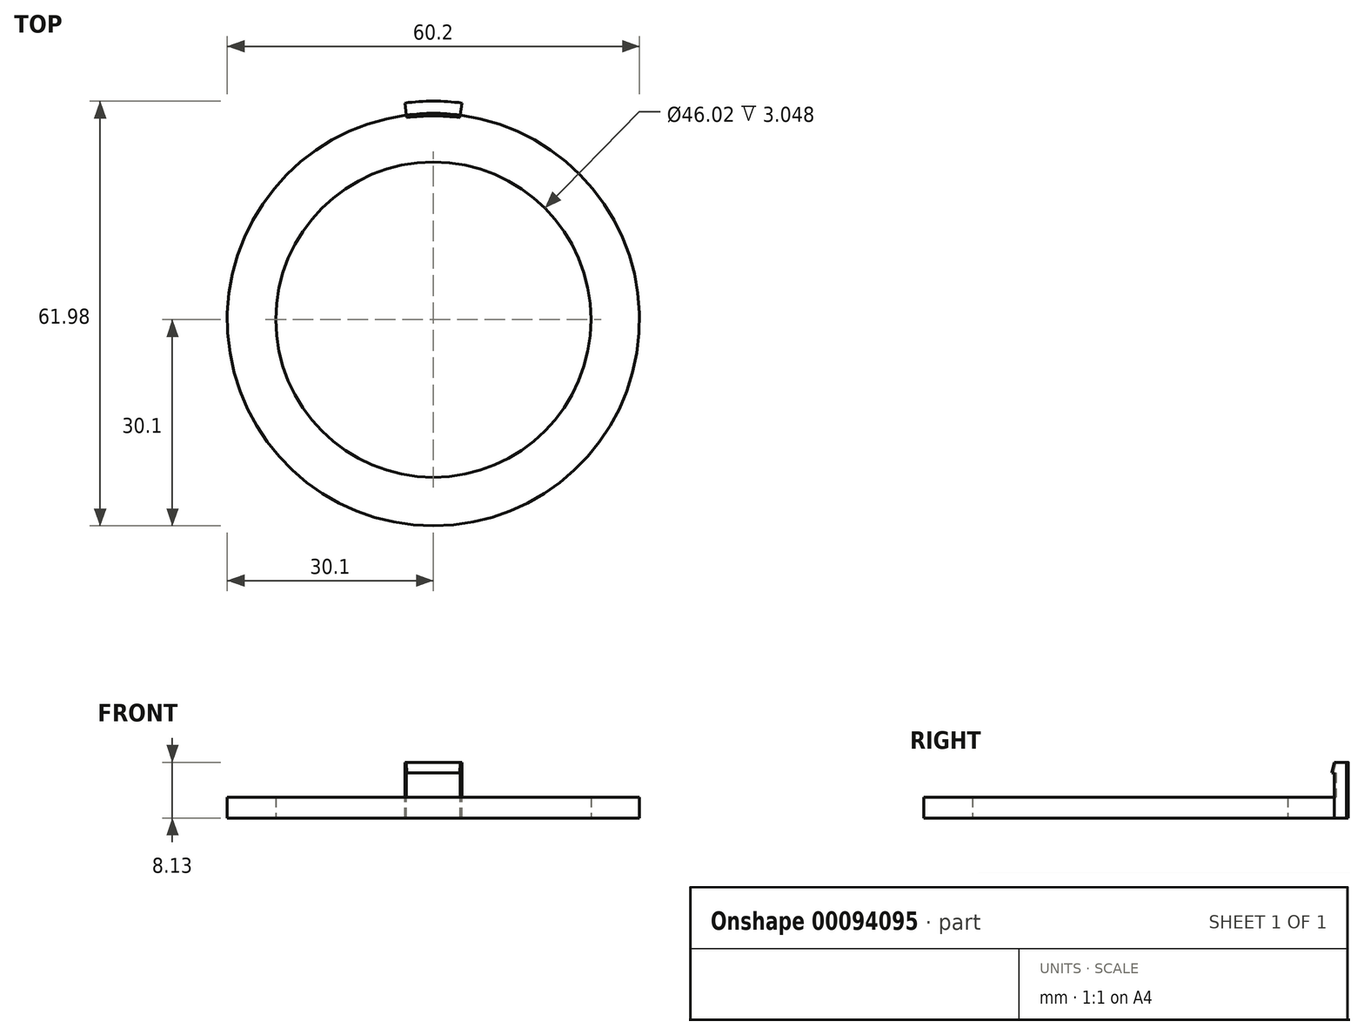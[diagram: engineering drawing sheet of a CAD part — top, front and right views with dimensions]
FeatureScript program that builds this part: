
annotation { "Feature Type Name" : "Feature", "Feature Type Description" : "" }
export const myFeature = defineFeature(function(context is Context, id is Id, definition is map)
    precondition{}
    {
        {
            var Q0;
            Q0=qCreatedBy(makeId("Top.planeOp"),FACE);
            var sketch = newSketch(context, id + "F0", { "sketchPlane" : qUnion([Q0])});
            skCircle(sketch, "E0", {"center": v(0, 0) * mm, "radius": 23.01 * mm});
            skCircle(sketch, "E1", {"center": v(0, 0) * mm, "radius": 30.1 * mm});
            skSolve(sketch);
        }
        {
            var Q0;
            Q0=makeQuery(id+"F0.imprint","IMPRINT",FACE,{"disambiguationData":[TD([[makeQuery(id+"F0.imprint","IMPRINT",EDGE,{"derivedFrom":sQuery(id+"F0.wireOp",EDGE,"E0")}),-1.0]])]});
            extrude(context, id + "F1", {"entities" : qUnion([Q0]), "depth" : 3.05 * mm, "offsetDistance" : 25.4 * mm});
        }
        {
            var Q0;
            Q0=qCreatedBy(makeId("Right.planeOp"),FACE);
            var sketch = newSketch(context, id + "F2", { "sketchPlane" : qUnion([Q0])});
            skLineSegment(sketch, "E2", {"start": v(-23.01, 3.05) * mm, "end": v(-30.1, 3.05) * mm});
            skLineSegment(sketch, "E3", {"start": v(30.1, 3.05) * mm, "end": v(23.01, 3.05) * mm});
            skLineSegment(sketch, "E4", {"start": v(30.1, 3.05) * mm, "end": v(30.1, 0) * mm});
            skLineSegment(sketch, "E5", {"start": v(-30.1, 0) * mm, "end": v(-30.1, 3.05) * mm});
            skLineSegment(sketch, "E6.bottom", {"start": v(30.1, 0) * mm, "end": v(31.88, 0) * mm});
            skLineSegment(sketch, "E6.top", {"start": v(30.1, 8.13) * mm, "end": v(31.88, 8.13) * mm});
            skLineSegment(sketch, "E6.left", {"start": v(30.1, 0) * mm, "end": v(30.1, 8.13) * mm});
            skLineSegment(sketch, "E6.right", {"start": v(31.88, 0) * mm, "end": v(31.88, 8.13) * mm});
            skLineSegment(sketch, "E7", {"start": v(30.1, 8.13) * mm, "end": v(29.72, 6.6) * mm});
            skLineSegment(sketch, "E8", {"start": v(29.72, 6.6) * mm, "end": v(30.1, 6.6) * mm});
            skSolve(sketch);
        }
        {
            var Q0;
            {var subQ3=sQuery(id+"F2.wireOp",EDGE,"E6.bottom");Q0=makeQuery(id+"F2.imprint","IMPRINT",FACE,{"disambiguationData":[TD([[makeQuery(id+"F2.imprint","IMPRINT",EDGE,{"derivedFrom":subQ3}),1.0]])]});}
            var Q1;
            {var subQ0=sQuery(id+"F2.wireOp",EDGE,"E7");Q1=makeQuery(id+"F2.imprint","IMPRINT",FACE,{"disambiguationData":[TD([[makeQuery(id+"F2.imprint","IMPRINT",EDGE,{"derivedFrom":subQ0}),1.0]])]});}
            var Q2;
            Q2=makeQuery(id+"F1.opExtrude","SWEPT_FACE",FACE,{"disambiguationData":[OSD([sQuery(id+"F0.wireOp",EDGE,"E0")])]});
            revolve(context, id + "F3", {"operationType" : NewBodyOperationType.ADD, "surfaceOperationType" : NewSurfaceOperationType.NEW, "entities" : qUnion([Q0, Q1]), "axis" : qUnion([Q2]), "revolveType" : RevolveType.SYMMETRIC, "angle" : 15 * degree});
        }
    });
